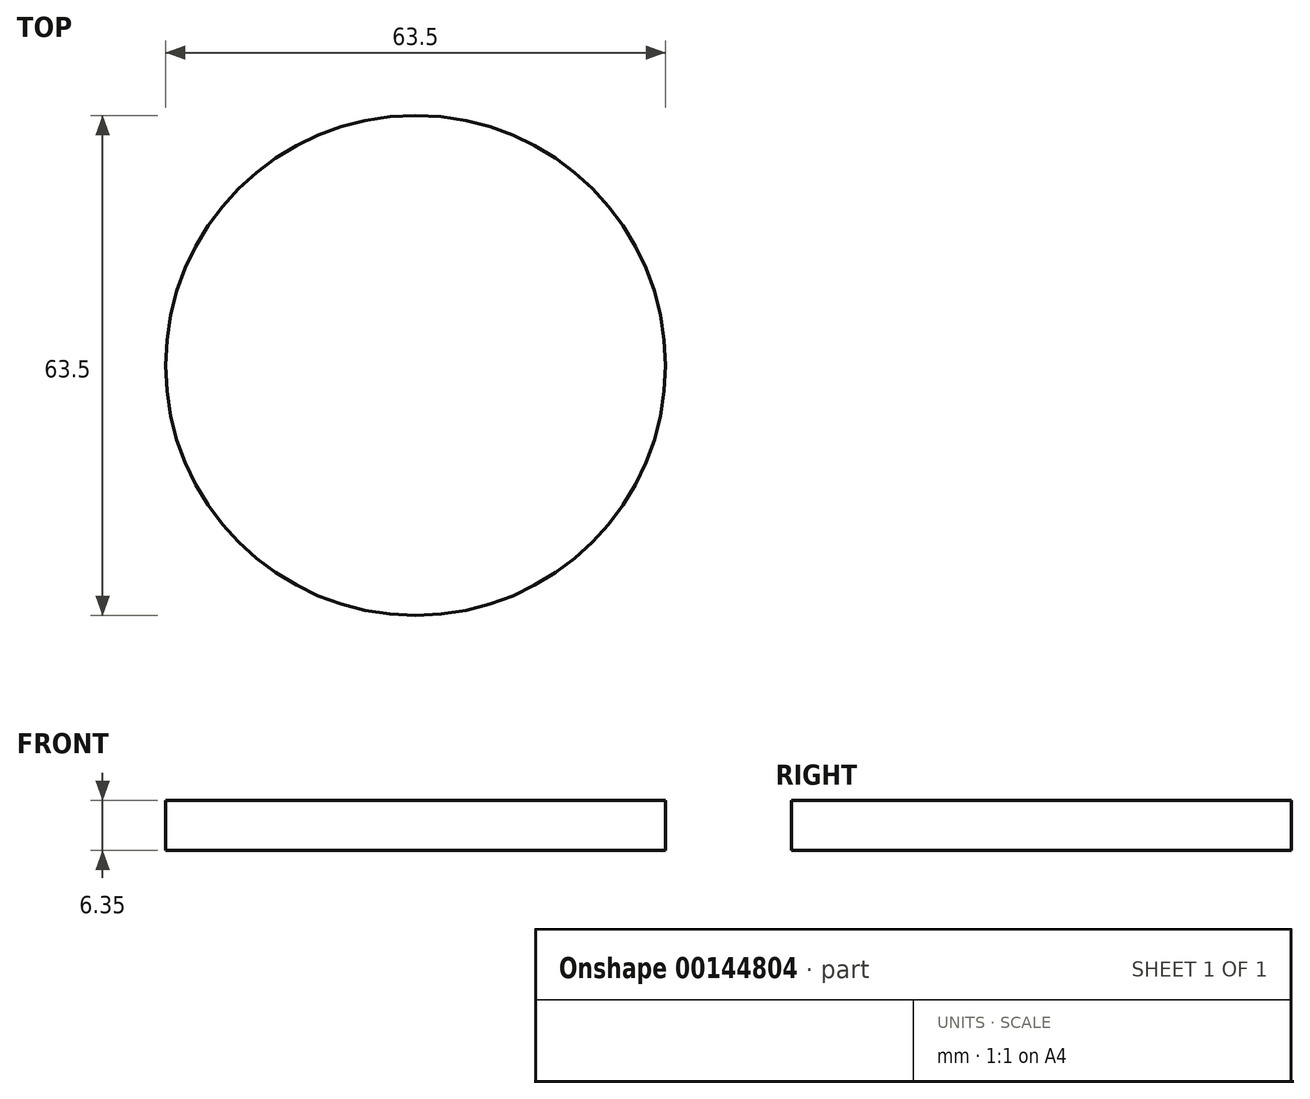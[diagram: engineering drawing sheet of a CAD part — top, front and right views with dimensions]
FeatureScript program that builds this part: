
annotation { "Feature Type Name" : "Feature", "Feature Type Description" : "" }
export const myFeature = defineFeature(function(context is Context, id is Id, definition is map)
    precondition{}
    {
        {
            var Q0;
            Q0=qCreatedBy(makeId("Top.planeOp"),FACE);
            var sketch = newSketch(context, id + "F0", { "sketchPlane" : qUnion([Q0])});
            skCircle(sketch, "E0", {"center": v(0, 0) * mm, "radius": 31.75 * mm});
            skSolve(sketch);
        }
        {
            var Q0;
            Q0 = qSketchRegion(id + "F0", true);
            extrude(context, id + "F1", {"entities" : qUnion([Q0]), "depth" : 6.35 * mm});
        }
    });
